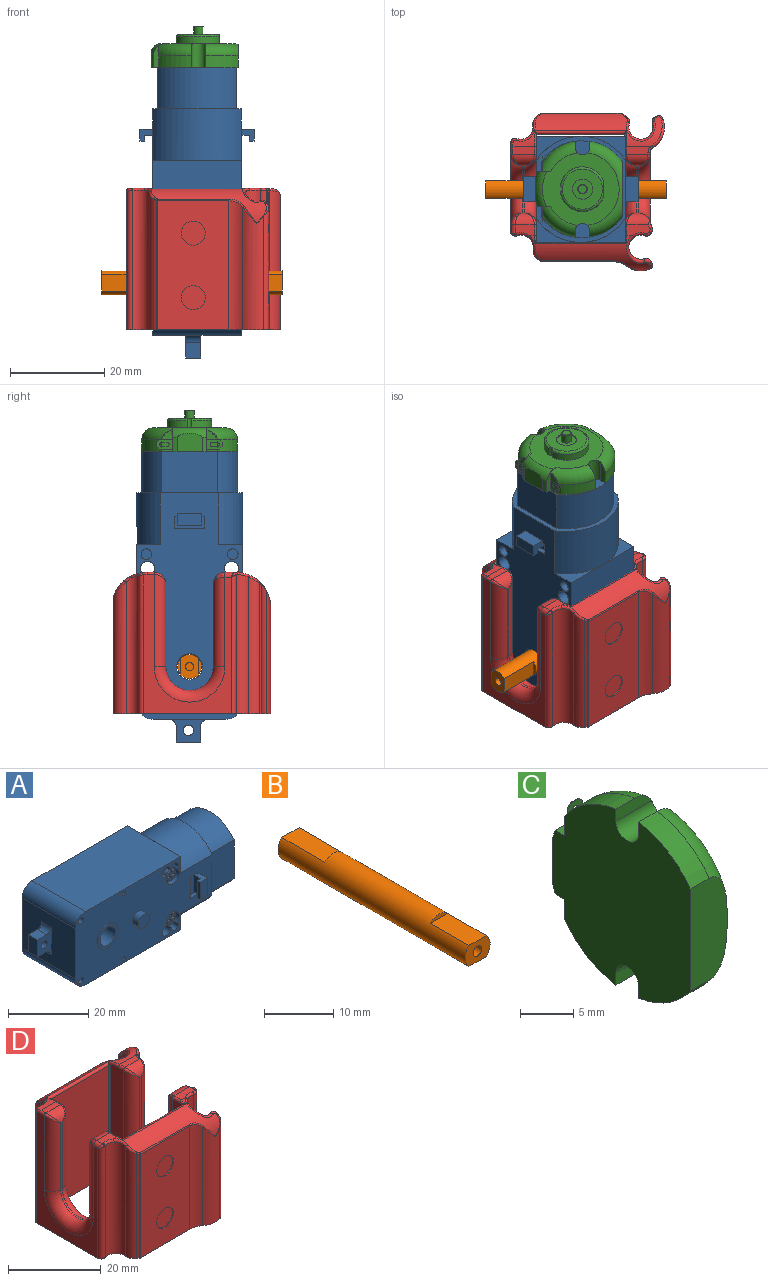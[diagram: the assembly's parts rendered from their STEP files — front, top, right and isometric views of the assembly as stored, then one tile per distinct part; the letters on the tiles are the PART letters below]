
ASSEMBLY  parts=4 mates=3
PART A: 126 faces, bbox 61.5x24.2x22.5 mm
  f0: torus R=1.4mm, axis (0,-1,0), area 4.7mm2, adj f2,f68
  f1: torus R=1.4mm, axis (0,-1,0), area 4.7mm2, adj f3,f66
  f2: cylinder r=1.7mm len=3.4mm, axis (0,1,0), area 12.8mm2, adj f0,f23,f67
  f3: cylinder r=1.7mm len=3.4mm, axis (0,1,0), area 12.8mm2, adj f1,f24,f65
  f4: cylinder r=2.25mm len=4.5mm, axis (0,-1,0), area 19.8mm2, adj f8,f9,f23,f26
  f5: cylinder r=2.25mm len=4.5mm, axis (0,-1,0), area 19.8mm2, adj f12,f13,f24,f26
  f6: cylinder r=1.12mm len=7.5mm, axis (0,1,0), area 53mm2, adj f37,f62
  f7: cylinder r=1.12mm len=7.5mm, axis (0,1,0), area 53mm2, adj f37,f61
  f8: cylinder r=1.5mm len=18.8mm, axis (0,-1,0), area 173.3mm2, adj f4,f23,f26,f37,f64
  f9: cylinder r=1.12mm len=7.5mm, axis (0,-1,0), area 48.7mm2, adj f4,f23,f26,f55,f64,f67
  f10: cylinder r=0.62mm len=7.5mm, axis (0,-1,0), area 29.5mm2, adj f26,f54
  f11: cylinder r=0.9mm len=7.5mm, axis (0,-1,0), area 42.4mm2, adj f26,f53
  f12: cylinder r=1.12mm len=7.5mm, axis (0,-1,0), area 48.7mm2, adj f5,f24,f26,f52,f63,f65
  f13: cylinder r=1.5mm len=18.8mm, axis (0,-1,0), area 173.3mm2, adj f5,f24,f26,f37,f63
  f14: cylinder r=0.62mm len=7.5mm, axis (0,-1,0), area 29.5mm2, adj f26,f51
  f15: cylinder r=0.9mm len=7.5mm, axis (0,-1,0), area 42.4mm2, adj f26,f50
  f16: cylinder r=2mm len=4mm, axis (0,1,0), area 25.1mm2, adj f26,f49
  f17: cylinder r=3.62mm len=7.25mm, axis (0,1,0), area 5.7mm2, adj f26,f48
  f18: cylinder r=2.75mm len=19.05mm, axis (0,1,0), area 329.2mm2, adj f37,f48
  f19: cylinder r=1.1mm len=3.2mm, axis (0,1,0), area 22.1mm2, adj f38,f40
  f20: plane 5.25x2.7mm, normal (-1,0,0), area 14.2mm2, adj f107,f113,f115,f125
  f21: plane 1x0.63mm, normal (-1,0,0), area 0.6mm2, adj f37,f109,f112,f118
  f22: plane 1x0.63mm, normal (-1,0,0), area 0.6mm2, adj f26,f103,f107,f113
  f23: plane 4.5x4.48mm, normal (0,-1,0), area 5.4mm2, adj f2,f4,f8,f9,f64
  f24: plane 4.5x4.48mm, normal (0,-1,0), area 5.4mm2, adj f3,f5,f12,f13,f63
  f25: plane 22.5x18.8mm, normal (1,0,0), area 66.1mm2, adj f26,f27,f37,f47,f56,f57,f58,f59
  f26: plane 48x22.3mm, normal (0,-1,0), area 823.8mm2, adj f4,f5,f8,f9,f10,f11,f12,f13
  f27: cylinder r=11.25mm len=18.8mm, axis (-1,0,0), area 244.8mm2, adj f25,f26,f28,f29,f37,f45
  f28: plane 7.9x4.97mm, normal (1,0,0), area 13.3mm2, adj f27,f33,f37
  f29: plane 7.9x4.97mm, normal (1,0,0), area 13.3mm2, adj f26,f27,f33
  f30: plane 7.9x4.97mm, normal (1,0,0), area 13.3mm2, adj f26,f36,f47
  f31: plane 7.9x4.97mm, normal (1,0,0), area 13.3mm2, adj f36,f37,f47
  f32: plane 18.8x15.3mm, normal (-1,0,0), area 261.4mm2, adj f26,f34,f35,f37,f38,f40,f43,f44
  f33: plane 33.5x18.8mm, normal (0,0,1), area 629.8mm2, adj f26,f28,f29,f34,f37,f45
  f34: cylinder r=3.5mm len=18.8mm, axis (0,1,0), area 103.4mm2, adj f26,f32,f33,f37
  f35: cylinder r=3.5mm len=18.8mm, axis (0,1,0), area 103.4mm2, adj f26,f32,f36,f37
  f36: plane 33.5x18.8mm, normal (0,0,-1), area 629.8mm2, adj f26,f30,f31,f35,f37,f46
  f37: plane 48x22.3mm, normal (0,1,0), area 890.3mm2, adj f6,f7,f8,f13,f18,f21,f25,f27
  f38: plane 8.2x4.8mm, normal (0,-1,0), area 22.1mm2, adj f19,f32,f39,f41,f42,f43,f44
  f39: plane 3.3x3.2mm, normal (0,0,1), area 10.6mm2, adj f38,f40,f42,f44
  f40: plane 8.2x4.8mm, normal (0,1,0), area 22.1mm2, adj f19,f32,f39,f41,f42,f43,f44
  f41: plane 3.3x3.2mm, normal (0,0,-1), area 10.6mm2, adj f38,f40,f42,f43
  f42: plane 5.2x3.2mm, normal (-1,0,0), area 16.6mm2, adj f38,f39,f40,f41
  f43: cylinder r=1.5mm len=3.2mm, axis (0,1,0), area 7.5mm2, adj f32,f38,f40,f41
  f44: cylinder r=1.5mm len=3.2mm, axis (0,-1,0), area 7.5mm2, adj f32,f38,f39,f40
  f45: plane 2.99x0.1mm, normal (-1,0,0), area 0.2mm2, adj f27,f33
  f46: plane 2.99x0.1mm, normal (-1,0,0), area 0.2mm2, adj f36,f47
  f47: cylinder r=11.25mm len=18.8mm, axis (-1,0,0), area 244.8mm2, adj f25,f26,f30,f31,f37,f46
  f48: plane 7.25x7.25mm, normal (0,-1,0), area 17.5mm2, adj f17,f18
  f49: plane 4x4mm, normal (0,-1,0), area 12.6mm2, adj f16
  f50: plane 1.8x1.8mm, normal (0,-1,0), area 2.5mm2, adj f15
  f51: plane 1.25x1.25mm, normal (0,-1,0), area 1.2mm2, adj f14
  f52: plane 2.25x2.25mm, normal (0,-1,0), area 4mm2, adj f12
  f53: plane 1.8x1.8mm, normal (0,-1,0), area 2.5mm2, adj f11
  f54: plane 1.25x1.25mm, normal (0,-1,0), area 1.2mm2, adj f10
  f55: plane 2.25x2.25mm, normal (0,-1,0), area 4mm2, adj f9
  f56: cylinder r=10.25mm len=16.8mm, axis (-1,0,0), area 172.1mm2, adj f25,f57,f59,f60
  f57: plane 11.75x8.74mm, normal (0,1,0), area 102.7mm2, adj f25,f56,f58,f60
  f58: cylinder r=10.25mm len=16.8mm, axis (-1,0,0), area 172.1mm2, adj f25,f57,f59,f60
  f59: plane 11.75x8.74mm, normal (0,-1,0), area 102.7mm2, adj f25,f56,f58,f60
  f60: plane 20.5x16.8mm, normal (1,0,0), area 300.5mm2, adj f56,f57,f58,f59
  f61: plane 2.25x2.25mm, normal (0,1,0), area 4mm2, adj f7
  f62: plane 2.25x2.25mm, normal (0,1,0), area 4mm2, adj f6
  f63: cylinder r=2.25mm len=2mm, axis (0,-1,0), area 0.9mm2, adj f12,f13,f24,f26
  f64: cylinder r=2.25mm len=2mm, axis (0,-1,0), area 0.9mm2, adj f8,f9,f23,f26
  f65: plane 0.76x0.22mm, normal (0,1,0), area 0.1mm2, adj f3,f12
  f66: plane 2.8x2.8mm, normal (0,-1,0), area 3.6mm2, adj f1,f69,f70,f71,f72,f73,f74,f75
  f67: plane 0.76x0.22mm, normal (0,1,0), area 0.1mm2, adj f2,f9
  f68: plane 2.8x2.8mm, normal (0,-1,0), area 3.6mm2, adj f0,f82,f83,f84,f85,f86,f87,f88
  f69: plane 1.5x0.84mm, normal (0.99,-0.16,0), area 0.9mm2, adj f66,f70,f81,f100
  f70: plane 1.5x0.6mm, normal (0,-0.16,-0.99), area 0.6mm2, adj f66,f69,f71,f81
  f71: plane 1.5x0.84mm, normal (-0.99,-0.16,0), area 0.9mm2, adj f66,f70,f81,f99
  f72: plane 1.5x0.84mm, normal (0,-0.16,-0.99), area 0.9mm2, adj f66,f73,f81,f99
  f73: plane 1.5x0.6mm, normal (-0.99,-0.16,0), area 0.6mm2, adj f66,f72,f74,f81
  f74: plane 1.5x0.84mm, normal (0,-0.16,0.99), area 0.9mm2, adj f66,f73,f81,f102
  f75: plane 1.5x0.84mm, normal (-0.99,-0.16,0), area 0.9mm2, adj f66,f76,f81,f102
  f76: plane 1.5x0.6mm, normal (0,-0.16,0.99), area 0.6mm2, adj f66,f75,f77,f81
  f77: plane 1.5x0.84mm, normal (0.99,-0.16,0), area 0.9mm2, adj f66,f76,f81,f101
  f78: plane 1.5x0.84mm, normal (0,-0.16,0.99), area 0.9mm2, adj f66,f79,f81,f101
  f79: plane 1.5x0.6mm, normal (0.99,-0.16,0), area 0.6mm2, adj f66,f78,f80,f81
  f80: plane 1.5x0.84mm, normal (0,-0.16,-0.99), area 0.9mm2, adj f66,f79,f81,f100
  f81: plane 1.93x1.93mm, normal (0,-1,0), area 0.5mm2, adj f69,f70,f71,f72,f73,f74,f75,f76
  f82: plane 1.5x0.84mm, normal (0,-0.16,0.99), area 0.9mm2, adj f68,f83,f94,f98
  f83: plane 1.5x0.6mm, normal (0.99,-0.16,0), area 0.6mm2, adj f68,f82,f84,f94
  f84: plane 1.5x0.84mm, normal (0,-0.16,-0.99), area 0.9mm2, adj f68,f83,f94,f96
  f85: plane 1.5x0.84mm, normal (0.99,-0.16,0), area 0.9mm2, adj f68,f86,f94,f96
  f86: plane 1.5x0.6mm, normal (0,-0.16,-0.99), area 0.6mm2, adj f68,f85,f87,f94
  f87: plane 1.5x0.84mm, normal (-0.99,-0.16,0), area 0.9mm2, adj f68,f86,f94,f95
  f88: plane 1.5x0.84mm, normal (0,-0.16,-0.99), area 0.9mm2, adj f68,f89,f94,f95
  f89: plane 1.5x0.6mm, normal (-0.99,-0.16,0), area 0.6mm2, adj f68,f88,f90,f94
  f90: plane 1.5x0.84mm, normal (0,-0.16,0.99), area 0.9mm2, adj f68,f89,f94,f97
  f91: plane 1.5x0.84mm, normal (-0.99,-0.16,0), area 0.9mm2, adj f68,f92,f94,f97
  f92: plane 1.5x0.6mm, normal (0,-0.16,0.99), area 0.6mm2, adj f68,f91,f93,f94
  f93: plane 1.5x0.84mm, normal (0.99,-0.16,0), area 0.9mm2, adj f68,f92,f94,f98
  f94: plane 1.93x1.93mm, normal (0,-1,0), area 0.5mm2, adj f82,f83,f84,f85,f86,f87,f88,f89
  f95: cylinder r=0.3mm len=1.54mm, axis (0.15,-0.98,0.15), area 0.7mm2, adj f68,f87,f88,f94
  f96: cylinder r=0.3mm len=1.54mm, axis (-0.15,-0.98,0.15), area 0.7mm2, adj f68,f84,f85,f94
  f97: cylinder r=0.3mm len=1.54mm, axis (0.15,-0.98,-0.15), area 0.7mm2, adj f68,f90,f91,f94
  f98: cylinder r=0.3mm len=1.54mm, axis (-0.15,-0.98,-0.15), area 0.7mm2, adj f68,f82,f93,f94
  f99: cylinder r=0.3mm len=1.54mm, axis (0.15,-0.98,0.15), area 0.7mm2, adj f66,f71,f72,f81
  f100: cylinder r=0.3mm len=1.54mm, axis (-0.15,-0.98,0.15), area 0.7mm2, adj f66,f69,f80,f81
  f101: cylinder r=0.3mm len=1.54mm, axis (-0.15,-0.98,-0.15), area 0.7mm2, adj f66,f77,f78,f81
  f102: cylinder r=0.3mm len=1.54mm, axis (0.15,-0.98,-0.15), area 0.7mm2, adj f66,f74,f75,f81
  f103: plane 2.5x1mm, normal (0,0,-1), area 2.5mm2, adj f22,f26,f106,f107
  f104: plane 1x0.63mm, normal (-1,0,0), area 0.6mm2, adj f26,f105,f107,f115
  f105: plane 2.5x1mm, normal (0,0,1), area 2.5mm2, adj f26,f104,f106,f107
  f106: plane 6.5x1mm, normal (1,0,0), area 6.5mm2, adj f26,f103,f105,f107
  f107: plane 6.5x2.5mm, normal (0,-1,0), area 12.8mm2, adj f20,f22,f103,f104,f105,f106,f113,f115
  f108: plane 1x0.63mm, normal (-1,0,0), area 0.6mm2, adj f37,f111,f112,f119
  f109: plane 2.5x1mm, normal (0,0,-1), area 2.5mm2, adj f21,f37,f110,f112
  f110: plane 6.5x1mm, normal (1,0,0), area 6.5mm2, adj f37,f109,f111,f112
  f111: plane 2.5x1mm, normal (0,0,1), area 2.5mm2, adj f37,f108,f110,f112
  f112: plane 6.5x2.5mm, normal (0,1,0), area 12.8mm2, adj f21,f108,f109,f110,f111,f118,f119,f120
  f113: plane 3.7x2.5mm, normal (0,0,1), area 5.4mm2, adj f20,f22,f26,f107,f114,f116,f124,f125
  f114: plane 5.25x2.7mm, normal (1,0,0), area 14.2mm2, adj f26,f113,f115,f116
  f115: plane 3.7x2.5mm, normal (0,0,-1), area 5.4mm2, adj f20,f26,f104,f107,f114,f116,f124,f125
  f116: plane 5.25x2.5mm, normal (0,-1,0), area 13.1mm2, adj f113,f114,f115,f124
  f117: plane 5.25x2.7mm, normal (1,0,0), area 14.2mm2, adj f37,f118,f119,f121
  f118: plane 3.7x2.5mm, normal (0,0,1), area 5.4mm2, adj f21,f37,f112,f117,f120,f121,f122,f123
  f119: plane 3.7x2.5mm, normal (0,0,-1), area 5.4mm2, adj f37,f108,f112,f117,f120,f121,f122,f123
  f120: plane 5.25x2.7mm, normal (-1,0,0), area 14.2mm2, adj f112,f118,f119,f123
  f121: plane 5.25x2.5mm, normal (0,1,0), area 13.1mm2, adj f117,f118,f119,f122
  f122: plane 5.25x1mm, normal (-1,0,0), area 5.3mm2, adj f118,f119,f121,f123
  f123: plane 5.25x1.2mm, normal (0,-1,0), area 6.3mm2, adj f118,f119,f120,f122
  f124: plane 5.25x1mm, normal (-1,0,0), area 5.2mm2, adj f113,f115,f116,f125
  f125: plane 5.25x1.2mm, normal (0,1,0), area 6.3mm2, adj f20,f113,f115,f124
PART B: 15 faces, bbox 5.1x38.2x5.1 mm
  f0: cylinder r=0.88mm len=8.75mm, axis (0,1,0), area 48.1mm2, adj f4,f14
  f1: cylinder r=0.88mm len=7.85mm, axis (0,-1,0), area 43.2mm2, adj f3,f5
  f2: cylinder r=2.55mm len=38.2mm, axis (0,1,0), area 483.5mm2, adj f3,f4,f6,f7,f8,f9,f10,f11
  f3: plane 5.1x3.7mm, normal (0,-1,0), area 14.6mm2, adj f1,f2,f6,f8
  f4: plane 5.1x3.7mm, normal (0,1,0), area 14.6mm2, adj f0,f2,f10,f12
  f5: plane 1.75x1.75mm, normal (0,-1,0), area 2.4mm2, adj f1
  f6: plane 7.85x3.51mm, normal (0,0,1), area 27.6mm2, adj f2,f3,f7
  f7: plane 3.51x0.7mm, normal (0,-1,0), area 1.7mm2, adj f2,f6
  f8: plane 7.85x3.51mm, normal (0,0,-1), area 27.6mm2, adj f2,f3,f9
  f9: plane 3.51x0.7mm, normal (0,-1,0), area 1.7mm2, adj f2,f8
  f10: plane 8.75x3.51mm, normal (0,0,1), area 30.7mm2, adj f2,f4,f11
  f11: plane 3.51x0.7mm, normal (0,1,0), area 1.7mm2, adj f2,f10
  f12: plane 8.75x3.51mm, normal (0,0,-1), area 30.7mm2, adj f2,f4,f13
  f13: plane 3.51x0.7mm, normal (0,1,0), area 1.7mm2, adj f2,f12
  f14: plane 1.75x1.75mm, normal (0,1,0), area 2.4mm2, adj f0
PART C: 61 faces, bbox 9.7x22.2x22.9 mm
  f0: cylinder r=0.43mm len=0.86mm, axis (0,-1,0), area 0.1mm2, adj f51,f52,f58,f60
  f1: cylinder r=0.43mm len=0.86mm, axis (0,-1,0), area 0.1mm2, adj f22,f40,f47,f48
  f2: torus R=0.9mm, axis (1,0,0), area 1mm2, adj f3,f37
  f3: cylinder r=1mm len=2mm, axis (-1,0,0), area 11.9mm2, adj f2,f16
  f4: cylinder r=2.12mm len=4.25mm, axis (1,0,0), area 2.7mm2, adj f16,f36
  f5: torus R=4.25mm, axis (1,0,0), area 20.7mm2, adj f6,f33,f34,f35,f36
  f6: cylinder r=0.5mm len=2mm, axis (-1,0,0), area 2.7mm2, adj f5,f13,f33,f34
  f7: plane 3.09x2.95mm, normal (0,1,0), area 3.3mm2, adj f9,f32,f53
  f8: plane 2.2x0.5mm, normal (0,1,0), area 1.1mm2, adj f9,f21,f29,f57
  f9: plane 5.29x3.04mm, normal (0,0,-1), area 4.7mm2, adj f7,f8,f13,f29,f32,f38,f50,f52
  f10: plane 1.54x0.86mm, normal (0,1,0), area 1.2mm2, adj f21,f58,f59,f60
  f11: plane 2.2x0.5mm, normal (0,1,0), area 1.1mm2, adj f15,f23,f29,f41
  f12: plane 3.09x2.95mm, normal (0,1,0), area 3.3mm2, adj f15,f30,f45
  f13: plane 16.23x15.36mm, normal (1,0,0), area 123.2mm2, adj f6,f9,f15,f19,f25,f30,f31,f32
  f14: plane 5.31x3.87mm, normal (0,1,0), area 19.3mm2, adj f29,f38,f49,f50
  f15: plane 5.29x3.04mm, normal (0,0,1), area 4.7mm2, adj f11,f12,f13,f29,f30,f38,f40,f41
  f16: plane 4.25x4.25mm, normal (1,0,0), area 11mm2, adj f3,f4
  f17: cylinder r=10.25mm len=6.9mm, axis (-1,0,0), area 20.9mm2, adj f18,f28,f29,f31
  f18: plane 4.85x1.51mm, normal (0,1,0), area 5.7mm2, adj f17,f19,f29,f31
  f19: cylinder r=1.5mm len=5mm, axis (-1,0,0), area 23.2mm2, adj f13,f18,f20,f29,f31,f32
  f20: plane 4.85x1.51mm, normal (0,-1,0), area 5.7mm2, adj f19,f21,f29,f32
  f21: cylinder r=10.25mm len=6.9mm, axis (-1,0,0), area 20.9mm2, adj f8,f10,f20,f29,f32,f51
  f22: plane 1.54x0.86mm, normal (0,1,0), area 1.2mm2, adj f1,f23,f47,f48
  f23: cylinder r=10.25mm len=6.9mm, axis (-1,0,0), area 20.9mm2, adj f11,f22,f24,f29,f30,f39
  f24: plane 4.85x1.51mm, normal (0,-1,0), area 5.7mm2, adj f23,f25,f29,f30
  f25: cylinder r=1.5mm len=5mm, axis (-1,0,0), area 23.2mm2, adj f13,f24,f26,f29,f30,f31
  f26: plane 4.85x1.51mm, normal (0,1,0), area 5.7mm2, adj f25,f27,f29,f31
  f27: cylinder r=10.25mm len=6.9mm, axis (-1,0,0), area 20.9mm2, adj f26,f28,f29,f31
  f28: plane 11.75x4.92mm, normal (0,-1,0), area 52.9mm2, adj f17,f27,f29,f31
  f29: plane 20.28x18.3mm, normal (-1,0,0), area 295.4mm2, adj f8,f9,f11,f14,f15,f17,f18,f19
  f30: torus R=7.75mm, axis (1,0,0), area 33.7mm2, adj f12,f13,f15,f23,f24,f25
  f31: torus R=7.75mm, axis (1,0,0), area 72.9mm2, adj f13,f17,f18,f19,f25,f26,f27,f28
  f32: torus R=7.75mm, axis (1,0,0), area 33.7mm2, adj f7,f9,f13,f19,f20,f21
  f33: cylinder r=4.75mm len=9.12mm, axis (-1,0,0), area 18.9mm2, adj f5,f6,f13,f35
  f34: cylinder r=4.75mm len=9.12mm, axis (-1,0,0), area 18.9mm2, adj f5,f6,f13,f35
  f35: plane 4.08x2.48mm, normal (0,-1,0), area 6.8mm2, adj f5,f13,f33,f34
  f36: plane 8.5x8.5mm, normal (1,0,0), area 42.6mm2, adj f4,f5
  f37: plane 1.8x1.8mm, normal (1,0,0), area 2.5mm2, adj f2
  f38: revolved ~8.87x2.61mm, area 18mm2, adj f9,f13,f14,f15,f49,f50
  f39: plane 2x1.03mm, normal (0,-1,0), area 1.5mm2, adj f23,f41,f42,f43,f44,f45,f46,f47
  f40: plane 3.23x2mm, normal (0,1,0), area 4.7mm2, adj f1,f15,f41,f42,f43,f44,f45,f46
  f41: plane 2.73x0.1mm, normal (-1,0,0), area 0.3mm2, adj f11,f15,f39,f40,f42
  f42: plane 0.5x0.5mm, normal (-0.71,0,0.71), area 0.1mm2, adj f39,f40,f41,f43
  f43: plane 1x0.1mm, normal (0,0,1), area 0.1mm2, adj f39,f40,f42,f44
  f44: plane 0.5x0.5mm, normal (0.71,0,0.71), area 0.1mm2, adj f39,f40,f43,f45
  f45: plane 2.73x0.1mm, normal (1,0,0), area 0.3mm2, adj f12,f15,f39,f40,f44
  f46: cylinder r=0.43mm len=0.86mm, axis (0,-1,0), area 0.1mm2, adj f39,f40,f47,f48
  f47: plane 1.14x0.1mm, normal (-1,0,0), area 0.1mm2, adj f1,f22,f39,f40,f46
  f48: plane 1.14x0.1mm, normal (1,0,0), area 0.1mm2, adj f1,f22,f39,f40,f46
  f49: cylinder r=10.25mm len=3mm, axis (1,0,0), area 3.2mm2, adj f14,f15,f29,f38
  f50: cylinder r=10.25mm len=3mm, axis (1,0,0), area 3.2mm2, adj f9,f14,f29,f38
  f51: plane 2x1.03mm, normal (0,-1,0), area 1.5mm2, adj f0,f21,f53,f54,f55,f56,f57,f58
  f52: plane 3.23x2mm, normal (0,1,0), area 4.7mm2, adj f0,f9,f53,f54,f55,f56,f57,f58
  f53: plane 2.73x0.1mm, normal (1,0,0), area 0.3mm2, adj f7,f9,f51,f52,f54
  f54: plane 0.5x0.5mm, normal (0.71,0,-0.71), area 0.1mm2, adj f51,f52,f53,f55
  f55: plane 1x0.1mm, normal (0,0,-1), area 0.1mm2, adj f51,f52,f54,f56
  f56: plane 0.5x0.5mm, normal (-0.71,0,-0.71), area 0.1mm2, adj f51,f52,f55,f57
  f57: plane 2.73x0.1mm, normal (-1,0,0), area 0.3mm2, adj f8,f9,f51,f52,f56
  f58: plane 1.14x0.1mm, normal (1,0,0), area 0.1mm2, adj f0,f10,f51,f52,f59
  f59: cylinder r=0.43mm len=0.86mm, axis (0,-1,0), area 0.1mm2, adj f10,f52,f58,f60
  f60: plane 1.14x0.1mm, normal (-1,0,0), area 0.1mm2, adj f0,f10,f51,f52,f59
PART D: 176 faces, bbox 32.6x33.5x33 mm
  f0: plane 27.35x15.09mm, normal (0,-1,0), area 372.1mm2, adj f1,f65,f140,f142,f172,f174
  f1: plane 33.4x32.6mm, normal (0,0,-1), area 425.3mm2, adj f0,f4,f5,f8,f9,f10,f11,f13
  f2: cylinder r=7.5mm len=4.5mm, axis (-1,0,0), area 7.3mm2, adj f7,f90,f133,f134,f135
  f3: cylinder r=7.5mm len=1.32mm, axis (-1,0,0), area 0.7mm2, adj f25,f83,f85
  f4: plane 29.5x22.12mm, normal (1,0,0), area 269.2mm2, adj f1,f34,f35,f37,f80,f83,f89,f90
  f5: plane 29.5x22.12mm, normal (-1,0,0), area 269.2mm2, adj f1,f46,f48,f49,f79,f81,f93,f94
  f6: plane 4.91x1.49mm, normal (0,0,1), area 6.8mm2, adj f32,f44,f67,f68,f93
  f7: plane 4.5x1.49mm, normal (0,0,1), area 6.7mm2, adj f2,f36,f89,f136
  f8: cylinder r=2.54mm len=29.4mm, axis (0,0,-1), area 149.3mm2, adj f1,f51,f112,f129,f131,f133
  f9: cylinder r=2.58mm len=29.5mm, axis (0,0,-1), area 152.9mm2, adj f1,f52,f82,f85,f108
  f10: plane 27.7x0.51mm, normal (-0.59,-0.81,0), area 17.2mm2, adj f1,f52,f87,f142
  f11: cylinder r=5mm len=25.89mm, axis (0,0,-1), area 112.4mm2, adj f1,f56,f65,f113,f138
  f12: plane 26.57x0.02mm, normal (0.81,0.59,0), area 0.7mm2, adj f54,f56,f115
  f13: cylinder r=2.58mm len=29.5mm, axis (0,0,-1), area 275.2mm2, adj f1,f54,f55,f117,f118
  f14: plane 29.5x0.09mm, normal (0.81,-0.59,0), area 3.4mm2, adj f1,f55,f60,f120
  f15: cylinder r=5mm len=29.49mm, axis (0,0,-1), area 187.6mm2, adj f1,f57,f61,f70
  f16: plane 26.32x0.05mm, normal (-0.59,0.81,0), area 1.7mm2, adj f1,f57,f58,f72
  f17: cylinder r=2.54mm len=27.31mm, axis (0,0,-1), area 259.4mm2, adj f1,f58,f59,f74
  f18: plane 26.32x1.1mm, normal (0.59,0.81,0), area 34.6mm2, adj f1,f59,f76,f123
  f19: plane 29.33x18.2mm, normal (0,1,0), area 533.7mm2, adj f1,f84,f98,f101
  f20: plane 28.73x18.2mm, normal (0,-1,0), area 522.9mm2, adj f1,f92,f95,f104
  f21: plane 24.55x15.81mm, normal (0,1,0), area 388mm2, adj f1,f50,f53,f126
  f22: plane 4.94x2.22mm, normal (0,0,1), area 9mm2, adj f33,f47,f79,f118,f119,f120,f121,f122
  f23: plane 29.5x18.7mm, normal (-1,0,0), area 170.2mm2, adj f1,f38,f40,f41,f108,f110,f112,f135
  f24: plane 29.5x14.12mm, normal (1,0,0), area 63.6mm2, adj f1,f42,f43,f61,f62,f67
  f25: plane 4x2.22mm, normal (0,0,1), area 7.6mm2, adj f3,f39,f80,f82,f107,f110
  f26: cylinder r=5mm len=10mm, axis (1,0,0), area 7.9mm2, adj f27,f28,f43,f48
  f27: plane 17.5x0.5mm, normal (0,1,0), area 8.8mm2, adj f26,f45,f47,f49
  f28: plane 17.5x0.5mm, normal (0,-1,0), area 8.8mm2, adj f26,f42,f44,f46
  f29: cylinder r=5mm len=10mm, axis (1,0,0), area 7.9mm2, adj f30,f31,f35,f40
  f30: plane 17.5x0.5mm, normal (0,-1,0), area 8.8mm2, adj f29,f34,f36,f38
  f31: plane 17.5x0.5mm, normal (0,1,0), area 8.8mm2, adj f29,f37,f39,f41
  f32: cylinder r=7.5mm len=27.03mm, axis (-1,0,0), area 132.1mm2, adj f6,f69,f70,f71,f72,f73,f74,f75
  f33: cylinder r=7.5mm len=24.46mm, axis (-1,0,0), area 103.7mm2, adj f22,f81,f84,f85,f86,f87,f113,f114
  f34: cylinder r=2.5mm len=19.5mm, axis (0,0,-1), area 72.6mm2, adj f4,f30,f35,f88
  f35: torus R=7.5mm, axis (1,0,0), area 72.9mm2, adj f4,f29,f34,f37
  f36: cylinder r=2.5mm len=4.5mm, axis (1,0,0), area 12mm2, adj f7,f30,f88,f137
  f37: cylinder r=2.5mm len=19.5mm, axis (0,0,1), area 72.6mm2, adj f4,f31,f35,f78
  f38: cylinder r=2.5mm len=19.5mm, axis (0,0,1), area 72.6mm2, adj f23,f30,f40,f137
  f39: cylinder r=2.5mm len=4mm, axis (-1,0,0), area 10.7mm2, adj f25,f31,f78,f111
  f40: torus R=7.5mm, axis (1,0,0), area 72.9mm2, adj f23,f29,f38,f41
  f41: cylinder r=2.5mm len=19mm, axis (0,0,-1), area 71.7mm2, adj f23,f31,f40,f111
  f42: cylinder r=2.5mm len=19.5mm, axis (0,0,-1), area 72.6mm2, adj f24,f28,f43,f66
  f43: torus R=7.5mm, axis (1,0,0), area 71.7mm2, adj f24,f26,f42,f45,f63
  f44: cylinder r=2.5mm len=4.5mm, axis (1,0,0), area 12mm2, adj f6,f28,f66,f91
  f45: cylinder r=2.5mm len=19.77mm, axis (0,0,1), area 63.2mm2, adj f27,f43,f47,f64,f121
  f46: cylinder r=2.5mm len=19.5mm, axis (0,0,1), area 72.6mm2, adj f5,f28,f48,f91
  f47: cylinder r=2.5mm len=4.77mm, axis (-1,0,0), area 12.5mm2, adj f22,f27,f45,f77,f121
  f48: torus R=7.5mm, axis (1,0,0), area 72.9mm2, adj f5,f26,f46,f49
  f49: cylinder r=2.5mm len=19.5mm, axis (0,0,-1), area 72.6mm2, adj f5,f27,f48,f77
  f50: cylinder r=2.5mm len=25.49mm, axis (0,0,-1), area 38.1mm2, adj f1,f21,f51,f127,f128
  f51: cylinder r=2.5mm len=27.85mm, axis (0,0,-1), area 69.2mm2, adj f1,f8,f50,f128
  f52: cylinder r=2.5mm len=28.9mm, axis (0,0,-1), area 74.7mm2, adj f1,f9,f10,f86
  f53: cylinder r=2.5mm len=24.66mm, axis (0,0,-1), area 11.7mm2, adj f1,f21,f123,f125
  f54: bspline ~31.28x1.33mm, area 40.5mm2, adj f1,f12,f13,f116
  f55: bspline ~33x1.33mm, area 44.7mm2, adj f1,f13,f14,f119
  f56: bspline ~30.45x1.85mm, area 62.3mm2, adj f1,f11,f12,f114
  f57: bspline ~30.12x1.85mm, area 65.2mm2, adj f1,f15,f16,f71
  f58: bspline ~30.96x1.33mm, area 40.5mm2, adj f1,f16,f17,f73
  f59: bspline ~30.96x1.33mm, area 40.5mm2, adj f1,f17,f18,f75
  f60: bspline ~33x1.59mm, area 36mm2, adj f1,f14,f62,f63,f64,f122
  f61: bspline ~33x1.03mm, area 36.6mm2, adj f1,f15,f24,f68,f69
  f62: cylinder r=5mm len=5.84mm, axis (0,0,-1), area 11.3mm2, adj f1,f24,f60,f63
  f63: bspline ~6.25x2.21mm, area 6mm2, adj f43,f60,f62,f64
  f64: cylinder r=5mm len=19.5mm, axis (0,0,-1), area 23.3mm2, adj f45,f60,f63,f121
  f65: cylinder r=5mm len=27.35mm, axis (0,0,-1), area 84.5mm2, adj f0,f1,f11,f139
  f66: bspline ~2.6x2.5mm, area 1.3mm2, adj f42,f44,f67
  f67: cylinder r=0.5mm len=0.5mm, axis (0,-1,0), area 0.3mm2, adj f6,f24,f66,f68
  f68: bspline ~1.54x0.83mm, area 0.8mm2, adj f6,f61,f67,f69
  f69: bspline ~1.03x0.93mm, area 0.4mm2, adj f32,f61,f68,f70
  f70: bspline ~7.07x4.5mm, area 6mm2, adj f15,f32,f69,f71
  f71: bspline ~1.89x1.37mm, area 1.2mm2, adj f32,f57,f70,f72
  f72: bspline ~0.34x0.33mm, area 0mm2, adj f16,f32,f71,f73
  f73: bspline ~1.58x1.53mm, area 1.1mm2, adj f32,f58,f72,f74
  f74: bspline ~6.09x5.09mm, area 8.6mm2, adj f17,f32,f73,f75
  f75: bspline ~1.52x1.5mm, area 1.1mm2, adj f32,f59,f74,f76
  f76: bspline ~1.93x1.39mm, area 0.8mm2, adj f18,f32,f75,f124
  f77: bspline ~2.89x2.5mm, area 1.3mm2, adj f47,f49,f79
  f78: bspline ~2.89x2.5mm, area 1.3mm2, adj f37,f39,f80
  f79: cylinder r=0.5mm len=2.22mm, axis (0,1,0), area 1.7mm2, adj f5,f22,f77,f81
  f80: cylinder r=0.5mm len=2.22mm, axis (0,-1,0), area 1.7mm2, adj f4,f25,f78,f83
  f81: torus R=7mm, axis (1,0,0), area 1mm2, adj f5,f33,f79,f103
  f82: torus R=3.08mm, axis (0,0,1), area 2.1mm2, adj f9,f25,f85,f107
  f83: torus R=7mm, axis (1,0,0), area 1mm2, adj f3,f4,f80,f85,f100
  f84: cylinder r=0.5mm len=19.54mm, axis (-1,0,0), area 16.7mm2, adj f19,f33,f85,f99,f100,f102,f103
  f85: bspline ~4.19x2.09mm, area 2.4mm2, adj f3,f9,f33,f82,f83,f84,f86,f100
  f86: bspline ~3.11x2.07mm, area 1.9mm2, adj f33,f52,f85,f87
  f87: bspline ~0.8x0.73mm, area 0.4mm2, adj f10,f33,f86,f141
  f88: bspline ~2.6x2.5mm, area 1.3mm2, adj f34,f36,f89
  f89: cylinder r=0.5mm len=1.49mm, axis (0,-1,0), area 1.2mm2, adj f4,f7,f88,f90
  f90: torus R=7mm, axis (1,0,0), area 2.4mm2, adj f2,f4,f89,f97,f132
  f91: bspline ~2.6x2.5mm, area 1.3mm2, adj f44,f46,f93
  f92: cylinder r=0.5mm len=19.53mm, axis (-1,0,0), area 19mm2, adj f20,f32,f96,f97,f105,f106,f130
  f93: cylinder r=0.5mm len=1.49mm, axis (0,1,0), area 1.2mm2, adj f5,f6,f91,f94
  f94: torus R=7mm, axis (1,0,0), area 2.4mm2, adj f5,f32,f93,f106
  f95: cylinder r=0.2mm len=28.73mm, axis (0,0,-1), area 9mm2, adj f1,f4,f20,f96
  f96: torus R=0.7mm, axis (1,0,0), area 0.1mm2, adj f4,f92,f95,f97
  f97: bspline ~0.89x0.7mm, area 0.2mm2, adj f90,f92,f96,f131
  f98: cylinder r=0.2mm len=29.33mm, axis (0,0,1), area 9.2mm2, adj f1,f4,f19,f99
  f99: torus R=0.7mm, axis (1,0,0), area 0mm2, adj f4,f84,f98,f100
  f100: bspline ~0.81x0.7mm, area 0.2mm2, adj f83,f84,f85,f99
  f101: cylinder r=0.2mm len=29.33mm, axis (0,0,-1), area 9.2mm2, adj f1,f5,f19,f102
  f102: torus R=0.7mm, axis (1,0,0), area 0mm2, adj f5,f84,f101,f103
  f103: bspline ~0.81x0.7mm, area 0.1mm2, adj f81,f84,f102
  f104: cylinder r=0.2mm len=28.73mm, axis (0,0,1), area 9mm2, adj f1,f5,f20,f105
  f105: torus R=0.7mm, axis (1,0,0), area 0.1mm2, adj f5,f92,f104,f106
  f106: bspline ~0.89x0.7mm, area 0.1mm2, adj f92,f94,f105
  f107: torus R=0.5mm, axis (0,0,1), area 0.2mm2, adj f25,f82,f108,f109
  f108: cylinder r=1mm len=29.5mm, axis (0,0,-1), area 56mm2, adj f1,f9,f23,f107,f109
  f109: bspline ~1.05x1mm, area 0.5mm2, adj f107,f108,f110
  f110: cylinder r=1mm len=1.85mm, axis (0,1,0), area 2.5mm2, adj f23,f25,f109,f111
  f111: bspline ~2.95x2.5mm, area 2.7mm2, adj f39,f41,f110
  f112: cylinder r=1mm len=29.45mm, axis (0,0,-1), area 56.4mm2, adj f1,f8,f23,f134
  f113: bspline ~1.81x1.5mm, area 0.1mm2, adj f11,f33,f114
  f114: bspline ~3.14x1.97mm, area 2.1mm2, adj f33,f56,f113,f115
  f115: bspline ~1.86x1.58mm, area 0mm2, adj f12,f33,f114,f116
  f116: bspline ~2.21x1.85mm, area 1.9mm2, adj f33,f54,f115,f117
  f117: bspline ~6.34x4.64mm, area 8.1mm2, adj f13,f33,f116,f118
  f118: torus R=3.08mm, axis (0,0,1), area 2mm2, adj f13,f22,f117,f119
  f119: bspline ~2.01x1.16mm, area 1mm2, adj f22,f55,f118,f120
  f120: cylinder r=0.5mm len=0.5mm, axis (-0.59,-0.81,0), area 0.1mm2, adj f14,f22,f119,f122
  f121: torus R=5.5mm, axis (0,0,1), area 1.1mm2, adj f22,f45,f47,f64,f122
  f122: bspline ~1.7x1.01mm, area 0.8mm2, adj f22,f60,f120,f121
  f123: cylinder r=0.5mm len=24.66mm, axis (0,0,-1), area 5.4mm2, adj f1,f18,f53,f124
  f124: sphere r=0.5mm, area 0mm2, adj f76,f123,f125
  f125: bspline ~0.79x0.43mm, area 0.1mm2, adj f32,f53,f124,f126
  f126: cylinder r=0.5mm len=15.81mm, axis (-1,0,0), area 2.3mm2, adj f21,f32,f125,f127
  f127: bspline ~1.76x1.51mm, area 0.4mm2, adj f32,f50,f126,f128
  f128: bspline ~3.25x2.78mm, area 2.1mm2, adj f32,f50,f51,f127,f129
  f129: bspline ~2.7x2.27mm, area 1.2mm2, adj f8,f32,f128,f130
  f130: sphere r=0.5mm, area 0mm2, adj f92,f129,f131
  f131: bspline ~0.73x0.71mm, area 0.1mm2, adj f8,f97,f130,f132
  f132: sphere r=0.5mm, area 0mm2, adj f90,f131,f133
  f133: bspline ~4.13x2.52mm, area 3mm2, adj f2,f8,f132,f134
  f134: bspline ~1.54x1.06mm, area 1.1mm2, adj f2,f112,f133,f135
  f135: torus R=7mm, axis (1,0,0), area 0.7mm2, adj f2,f23,f134,f136
  f136: cylinder r=0.5mm len=1.49mm, axis (0,1,0), area 1.2mm2, adj f7,f23,f135,f137
  f137: bspline ~2.6x2.5mm, area 1.3mm2, adj f36,f38,f136
  f138: bspline ~4.79x3.84mm, area 0.6mm2, adj f11,f33,f139
  f139: bspline ~4.61x2.66mm, area 1.5mm2, adj f33,f65,f138,f140
  f140: cylinder r=0.5mm len=15.09mm, axis (-1,0,0), area 5.8mm2, adj f0,f33,f139,f141
  f141: sphere r=0.5mm, area 0.1mm2, adj f87,f140,f142
  f142: cylinder r=0.5mm len=27.35mm, axis (0,0,-1), area 8.6mm2, adj f0,f1,f10,f141
  f143: plane 3.29x0.5mm, normal (1,0,0), area 1.6mm2, adj f1,f144,f150,f151
  f144: plane 0.85x0.5mm, normal (0,1,0), area 0.4mm2, adj f1,f143,f145,f151
  f145: plane 3.29x0.5mm, normal (-1,0,0), area 1.6mm2, adj f1,f144,f146,f151
  f146: plane 1.09x0.5mm, normal (0,1,0), area 0.5mm2, adj f1,f145,f147,f151
  f147: plane 0.71x0.5mm, normal (-1,0,0), area 0.4mm2, adj f1,f146,f148,f151
  f148: plane 3.02x0.5mm, normal (0,-1,0), area 1.5mm2, adj f1,f147,f149,f151
  f149: plane 0.71x0.5mm, normal (1,0,0), area 0.4mm2, adj f1,f148,f150,f151
  f150: plane 1.09x0.5mm, normal (0,1,0), area 0.5mm2, adj f1,f143,f149,f151
  f151: plane 4x3.02mm, normal (0,0,-1), area 4.9mm2, adj f143,f144,f145,f146,f147,f148,f149,f150
  f152: plane 0.78x0.5mm, normal (0,1,0), area 0.4mm2, adj f1,f153,f170,f171
  f153: plane 3.14x0.96mm, normal (-0.96,0.29,0), area 1.6mm2, adj f1,f152,f154,f171
  f154: plane 0.5x0.02mm, normal (0,1,0), area 0mm2, adj f1,f153,f155,f171
  f155: extruded ~1.28x0.5mm, area 0.6mm2, adj f1,f154,f156,f171
  f156: plane 1.86x0.5mm, normal (1,0,0), area 0.9mm2, adj f1,f155,f157,f171
  f157: plane 0.76x0.5mm, normal (0,1,0), area 0.4mm2, adj f1,f156,f158,f171
  f158: plane 4x0.5mm, normal (-1,0,0), area 2mm2, adj f1,f157,f159,f171
  f159: plane 1.15x0.5mm, normal (0,-1,0), area 0.6mm2, adj f1,f158,f160,f171
  f160: plane 3.06x0.95mm, normal (0.96,-0.3,0), area 1.6mm2, adj f1,f159,f161,f171
  f161: plane 0.5x0.02mm, normal (0,-1,0), area 0mm2, adj f1,f160,f162,f171
  f162: plane 3.06x1mm, normal (-0.95,-0.31,0), area 1.6mm2, adj f1,f161,f163,f171
  f163: plane 1.15x0.5mm, normal (0,-1,0), area 0.6mm2, adj f1,f162,f164,f171
  f164: plane 4x0.5mm, normal (1,0,0), area 2mm2, adj f1,f163,f165,f171
  f165: plane 0.79x0.5mm, normal (0,1,0), area 0.4mm2, adj f1,f164,f166,f171
  f166: plane 1.89x0.5mm, normal (-1,0,0), area 0.9mm2, adj f1,f165,f167,f171
  f167: extruded ~0.5x0.31mm, area 0.2mm2, adj f1,f166,f168,f171
  f168: extruded ~0.93x0.5mm, area 0.5mm2, adj f1,f167,f169,f171
  f169: plane 0.5x0.02mm, normal (0,1,0), area 0mm2, adj f1,f168,f170,f171
  f170: plane 3.13x1.03mm, normal (0.95,0.31,0), area 1.6mm2, adj f1,f152,f169,f171
  f171: plane 4.27x4mm, normal (0,0,-1), area 11mm2, adj f152,f153,f154,f155,f156,f157,f158,f159
  f172: cylinder r=2.54mm len=5.08mm, axis (0,-1,0), area 4.8mm2, adj f0,f173
  f173: plane 5.08x5.08mm, normal (0,-1,0), area 20.3mm2, adj f172
  f174: cylinder r=2.54mm len=5.08mm, axis (0,-1,0), area 4.8mm2, adj f0,f175
  f175: plane 5.08x5.08mm, normal (0,-1,0), area 20.3mm2, adj f174
PLACE A rot(axis=(0.58,-0.58,0.58),120deg) t=(151.6,29.51,48.2)mm
PLACE B rot(axis=(0.58,-0.58,0.58),120deg) t=(150.55,29.51,48.2)mm
PLACE C rot(axis=(0.58,-0.58,0.58),120deg) t=(151.93,29.51,48.2)mm
PLACE D t=(162.48,6.15,12.35)mm
MATE fastened B.f0 <-> A.f17  axis (-1,0,0) through (149.6,18.36,22.35)mm
MATE fastened A.f17 <-> D.f26  axis (-1,0,0) through (151.6,18.36,22.35)mm
MATE fastened A.f27 <-> C.f29  axis (0,0,1) through (161,18.36,67.94)mm
